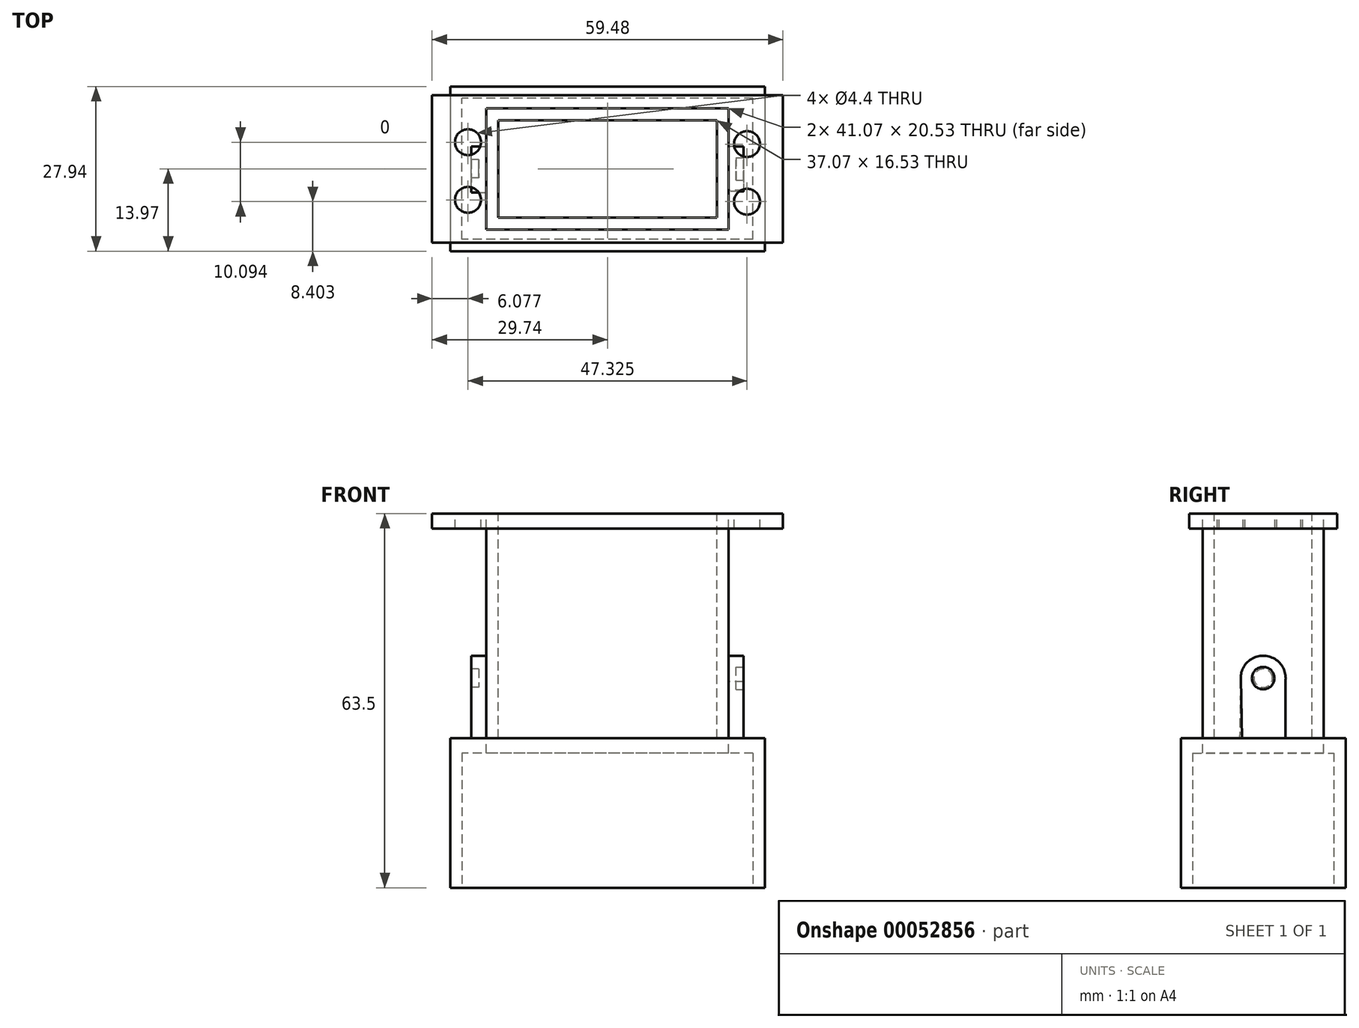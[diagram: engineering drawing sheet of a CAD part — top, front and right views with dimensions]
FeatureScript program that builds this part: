
annotation { "Feature Type Name" : "Feature", "Feature Type Description" : "" }
export const myFeature = defineFeature(function(context is Context, id is Id, definition is map)
    precondition{}
    {
        {
            var Q0;
            Q0=qCreatedBy(makeId("Top.planeOp"),FACE);
            var sketch = newSketch(context, id + "F0", { "sketchPlane" : qUnion([Q0])});
            skLineSegment(sketch, "E0.bottom", {"start": v(20.53, 10.27) * mm, "end": v(-20.53, 10.27) * mm});
            skLineSegment(sketch, "E0.top", {"start": v(20.53, -10.27) * mm, "end": v(-20.53, -10.27) * mm});
            skLineSegment(sketch, "E0.left", {"start": v(20.53, 10.27) * mm, "end": v(20.53, -10.27) * mm});
            skLineSegment(sketch, "E0.right", {"start": v(-20.53, 10.27) * mm, "end": v(-20.53, -10.27) * mm});
            skPoint(sketch, "E0.middle", {"position": v(0, 0) * mm});
            skSolve(sketch);
        }
        {
            var Q0;
            Q0=makeQuery(id+"F0.imprint","IMPRINT",FACE,{"disambiguationData":[TD([[makeQuery(id+"F0.imprint","IMPRINT",EDGE,{"derivedFrom":sQuery(id+"F0.wireOp",EDGE,"E0.bottom")}),1.0]])]});
            extrude(context, id + "F1", {"entities" : qUnion([Q0]), "oppositeDirection" : true, "depth" : 38.1 * mm});
        }
        {
            var Q0;
            Q0=makeQuery(id+"F1.opExtrude","CAP_FACE",FACE,{"disambiguationData":[OSD([sQuery(id+"F0.wireOp",EDGE,"E0.bottom"),sQuery(id+"F0.wireOp",EDGE,"E0.top"),sQuery(id+"F0.wireOp",EDGE,"E0.left"),sQuery(id+"F0.wireOp",EDGE,"E0.right")])],"isStart":false});
            var sketch = newSketch(context, id + "F2", { "sketchPlane" : qUnion([Q0])});
            skLineSegment(sketch, "E1.bottom", {"start": v(26.67, -13.97) * mm, "end": v(-26.67, -13.97) * mm});
            skLineSegment(sketch, "E1.top", {"start": v(26.67, 13.97) * mm, "end": v(-26.67, 13.97) * mm});
            skLineSegment(sketch, "E1.left", {"start": v(26.67, -13.97) * mm, "end": v(26.67, 13.97) * mm});
            skLineSegment(sketch, "E1.right", {"start": v(-26.67, -13.97) * mm, "end": v(-26.67, 13.97) * mm});
            skPoint(sketch, "E1.middle", {"position": v(0, 0) * mm});
            skSolve(sketch);
        }
        {
            var Q0;
            Q0=makeQuery(id+"F2.imprint","IMPRINT",FACE,{"disambiguationData":[TD([[makeQuery(id+"F2.imprint","IMPRINT",EDGE,{"derivedFrom":sQuery(id+"F2.wireOp",EDGE,"E1.bottom")}),-1.0]])]});
            extrude(context, id + "F3", {"entities" : qUnion([Q0]), "depth" : 25.4 * mm});
        }
        {
            var Q0;
            Q0=makeQuery(id+"F1.opExtrude","SWEPT_FACE",FACE,{"disambiguationData":[OSD([sQuery(id+"F0.wireOp",EDGE,"E0.right")])]});
            var sketch = newSketch(context, id + "F4", { "sketchPlane" : qUnion([Q0])});
            skCircle(sketch, "E2", {"center": v(0, -27.94) * mm, "radius": 3.81 * mm});
            skLineSegment(sketch, "E3", {"start": v(-3.8, -27.96) * mm, "end": v(-3.8, -38.1) * mm});
            skLineSegment(sketch, "E4", {"start": v(3.8, -27.87) * mm, "end": v(4, -38.1) * mm});
            skSolve(sketch);
        }
        {
            var Q0;
            {var subQ0=sQuery(id+"F4.wireOp",EDGE,"E3");Q0=makeQuery(id+"F4.imprint","IMPRINT",FACE,{"disambiguationData":[TD([[makeQuery(id+"F4.imprint","IMPRINT",EDGE,{"derivedFrom":subQ0}),1.0]])]});}
            var Q1;
            {var subQ0=sQuery(id+"F4.wireOp",EDGE,"E2");var subQ1=makeQuery(id+"F4.imprint","INTERSECT",VERTEX,{"derivedFrom":[subQ0,sQuery(id+"F4.wireOp",EDGE,"E3")]});Q1=makeQuery(id+"F4.imprint","IMPRINT",FACE,{"disambiguationData":[TD([[makeQuery(id+"F4.imprint","IMPRINT",EDGE,{"disambiguationData":[TD([[subQ1,1.0]])],"derivedFrom":subQ0}),1.0]])]});}
            extrude(context, id + "F5", {"entities" : qUnion([Q0, Q1]), "depth" : 2.54 * mm});
        }
        {
            var Q0;
            Q0=makeQuery(id+"F5.opExtrude","CAP_FACE",FACE,{"disambiguationData":[OSD([sQuery(id+"F0.wireOp",EDGE,"E0.right"),sQuery(id+"F4.wireOp",EDGE,"E2"),sQuery(id+"F4.wireOp",EDGE,"E3"),sQuery(id+"F4.wireOp",EDGE,"E4")])],"isStart":false});
            var sketch = newSketch(context, id + "F6", { "sketchPlane" : qUnion([Q0])});
            skCircle(sketch, "E5", {"center": v(0, -27.94) * mm, "radius": 1.56 * mm});
            skSolve(sketch);
        }
        {
            var Q0;
            Q0=makeQuery(id+"F6.imprint","IMPRINT",FACE,{"disambiguationData":[TD([[makeQuery(id+"F6.imprint","IMPRINT",EDGE,{"derivedFrom":sQuery(id+"F6.wireOp",EDGE,"E5")}),1.0]])]});
            extrude(context, id + "F7", {"entities" : qUnion([Q0]), "operationType" : NewBodyOperationType.REMOVE, "oppositeDirection" : true, "depth" : 1.27 * mm});
        }
        {
            var Q0;
            Q0=makeQuery(id+"F1.opExtrude","SWEPT_FACE",FACE,{"disambiguationData":[OSD([sQuery(id+"F0.wireOp",EDGE,"E0.left")])]});
            var sketch = newSketch(context, id + "F8", { "sketchPlane" : qUnion([Q0])});
            skCircle(sketch, "E6", {"center": v(0, -27.94) * mm, "radius": 3.81 * mm});
            skLineSegment(sketch, "E7", {"start": v(-3.8, -28.02) * mm, "end": v(-3.6, -38.1) * mm});
            skLineSegment(sketch, "E8", {"start": v(3.77, -28.51) * mm, "end": v(3.77, -38.1) * mm});
            skSolve(sketch);
        }
        {
            var Q0;
            {var subQ0=sQuery(id+"F8.wireOp",EDGE,"E6");var subQ1=makeQuery(id+"F8.imprint","INTERSECT",VERTEX,{"derivedFrom":[subQ0,sQuery(id+"F8.wireOp",EDGE,"E7")]});Q0=makeQuery(id+"F8.imprint","IMPRINT",FACE,{"disambiguationData":[TD([[makeQuery(id+"F8.imprint","IMPRINT",EDGE,{"disambiguationData":[TD([[subQ1,-1.0]])],"derivedFrom":subQ0}),1.0]])]});}
            var Q1;
            {var subQ0=sQuery(id+"F8.wireOp",EDGE,"E7");Q1=makeQuery(id+"F8.imprint","IMPRINT",FACE,{"disambiguationData":[TD([[makeQuery(id+"F8.imprint","IMPRINT",EDGE,{"derivedFrom":subQ0}),1.0]])]});}
            extrude(context, id + "F9", {"entities" : qUnion([Q0, Q1]), "depth" : 2.54 * mm});
        }
        {
            var Q0;
            Q0=makeQuery(id+"F9.opExtrude","CAP_FACE",FACE,{"disambiguationData":[OSD([sQuery(id+"F0.wireOp",EDGE,"E0.left"),sQuery(id+"F8.wireOp",EDGE,"E6"),sQuery(id+"F8.wireOp",EDGE,"E7"),sQuery(id+"F8.wireOp",EDGE,"E8")])],"isStart":false});
            var sketch = newSketch(context, id + "F10", { "sketchPlane" : qUnion([Q0])});
            skCircle(sketch, "E9", {"center": v(0, -27.94) * mm, "radius": 1.9 * mm});
            skSolve(sketch);
        }
        {
            var Q0;
            Q0=makeQuery(id+"F10.imprint","IMPRINT",FACE,{"disambiguationData":[TD([[makeQuery(id+"F10.imprint","IMPRINT",EDGE,{"derivedFrom":sQuery(id+"F10.wireOp",EDGE,"E9")}),1.0]])]});
            extrude(context, id + "F11", {"entities" : qUnion([Q0]), "operationType" : NewBodyOperationType.REMOVE, "oppositeDirection" : true, "depth" : 1.27 * mm});
        }
        {
            var Q0;
            Q0=makeQuery(id+"F1.opExtrude","CAP_FACE",FACE,{"disambiguationData":[OSD([sQuery(id+"F0.wireOp",EDGE,"E0.bottom"),sQuery(id+"F0.wireOp",EDGE,"E0.top"),sQuery(id+"F0.wireOp",EDGE,"E0.left"),sQuery(id+"F0.wireOp",EDGE,"E0.right")])],"isStart":true});
            var sketch = newSketch(context, id + "F12", { "sketchPlane" : qUnion([Q0])});
            skLineSegment(sketch, "E10.bottom", {"start": v(-29.74, -12.51) * mm, "end": v(29.74, -12.51) * mm});
            skLineSegment(sketch, "E10.top", {"start": v(-29.74, 12.51) * mm, "end": v(29.74, 12.51) * mm});
            skLineSegment(sketch, "E10.left", {"start": v(-29.74, -12.51) * mm, "end": v(-29.74, 12.51) * mm});
            skLineSegment(sketch, "E10.right", {"start": v(29.74, -12.51) * mm, "end": v(29.74, 12.51) * mm});
            skPoint(sketch, "E10.middle", {"position": v(0, 0) * mm});
            skCircle(sketch, "E11", {"center": v(23.66, -5.57) * mm, "radius": 2.2 * mm});
            skCircle(sketch, "E12", {"center": v(-23.66, -5.25) * mm, "radius": 2.2 * mm});
            skCircle(sketch, "E13", {"center": v(23.66, 4.21) * mm, "radius": 2.2 * mm});
            skCircle(sketch, "E14", {"center": v(-23.66, 4.53) * mm, "radius": 2.2 * mm});
            skSolve(sketch);
        }
        {
            var Q0;
            Q0=makeQuery(id+"F12.imprint","IMPRINT",FACE,{"disambiguationData":[TD([[makeQuery(id+"F12.imprint","IMPRINT",EDGE,{"derivedFrom":sQuery(id+"F12.wireOp",EDGE,"E10.bottom")}),1.0]])]});
            extrude(context, id + "F13", {"entities" : qUnion([Q0]), "oppositeDirection" : true, "depth" : 2.54 * mm});
        }
        {
            var Q0;
            Q0=makeQuery(id+"F1.opExtrude","CAP_FACE",FACE,{"disambiguationData":[OSD([sQuery(id+"F0.wireOp",EDGE,"E0.bottom"),sQuery(id+"F0.wireOp",EDGE,"E0.top"),sQuery(id+"F0.wireOp",EDGE,"E0.left"),sQuery(id+"F0.wireOp",EDGE,"E0.right")])],"isStart":true});
            var sketch = newSketch(context, id + "F14", { "sketchPlane" : qUnion([Q0])});
            skLineSegment(sketch, "E15.bottom", {"start": v(-18.53, -8.27) * mm, "end": v(18.53, -8.27) * mm});
            skLineSegment(sketch, "E15.top", {"start": v(-18.53, 8.27) * mm, "end": v(18.53, 8.27) * mm});
            skLineSegment(sketch, "E15.left", {"start": v(-18.53, -8.27) * mm, "end": v(-18.53, 8.27) * mm});
            skLineSegment(sketch, "E15.right", {"start": v(18.53, -8.27) * mm, "end": v(18.53, 8.27) * mm});
            skPoint(sketch, "E15.middle", {"position": v(0, 0) * mm});
            skSolve(sketch);
        }
        {
            var Q0;
            Q0=makeQuery(id+"F14.imprint","IMPRINT",FACE,{"disambiguationData":[TD([[makeQuery(id+"F14.imprint","IMPRINT",EDGE,{"derivedFrom":sQuery(id+"F14.wireOp",EDGE,"E15.bottom")}),1.0]])]});
            extrude(context, id + "F15", {"entities" : qUnion([Q0]), "operationType" : NewBodyOperationType.REMOVE, "endBound" : BoundingType.THROUGH_ALL, "oppositeDirection" : true, "depth" : 25.4 * mm});
        }
        {
            var Q0;
            Q0=makeQuery(id+"F3.opExtrude","CAP_FACE",FACE,{"disambiguationData":[OSD([sQuery(id+"F0.wireOp",EDGE,"E0.bottom"),sQuery(id+"F0.wireOp",EDGE,"E0.top"),sQuery(id+"F0.wireOp",EDGE,"E0.left"),sQuery(id+"F0.wireOp",EDGE,"E0.right"),sQuery(id+"F2.wireOp",EDGE,"E1.bottom"),sQuery(id+"F2.wireOp",EDGE,"E1.top"),sQuery(id+"F2.wireOp",EDGE,"E1.left"),sQuery(id+"F2.wireOp",EDGE,"E1.right")])],"isStart":false});
            var sketch = newSketch(context, id + "F16", { "sketchPlane" : qUnion([Q0])});
            skLineSegment(sketch, "E16.bottom", {"start": v(24.67, 11.97) * mm, "end": v(-24.67, 11.97) * mm});
            skLineSegment(sketch, "E16.top", {"start": v(24.67, -11.97) * mm, "end": v(-24.67, -11.97) * mm});
            skLineSegment(sketch, "E16.left", {"start": v(24.67, 11.97) * mm, "end": v(24.67, -11.97) * mm});
            skLineSegment(sketch, "E16.right", {"start": v(-24.67, 11.97) * mm, "end": v(-24.67, -11.97) * mm});
            skPoint(sketch, "E16.middle", {"position": v(0, 0) * mm});
            skSolve(sketch);
        }
        {
            var Q0;
            Q0=makeQuery(id+"F16.imprint","IMPRINT",FACE,{"disambiguationData":[TD([[makeQuery(id+"F16.imprint","IMPRINT",EDGE,{"derivedFrom":sQuery(id+"F16.wireOp",EDGE,"E16.bottom")}),1.0]])]});
            var Q1;
            Q1=makeQuery(id+"F1.opExtrude","CAP_FACE",FACE,{"disambiguationData":[OSD([sQuery(id+"F0.wireOp",EDGE,"E0.bottom"),sQuery(id+"F0.wireOp",EDGE,"E0.top"),sQuery(id+"F0.wireOp",EDGE,"E0.left"),sQuery(id+"F0.wireOp",EDGE,"E0.right")])],"isStart":false});
            extrude(context, id + "F17", {"entities" : qUnion([Q0]), "operationType" : NewBodyOperationType.REMOVE, "oppositeDirection" : true, "endBoundEntityFace" : qUnion([Q1]), "depth" : 22.86 * mm});
        }
    });
